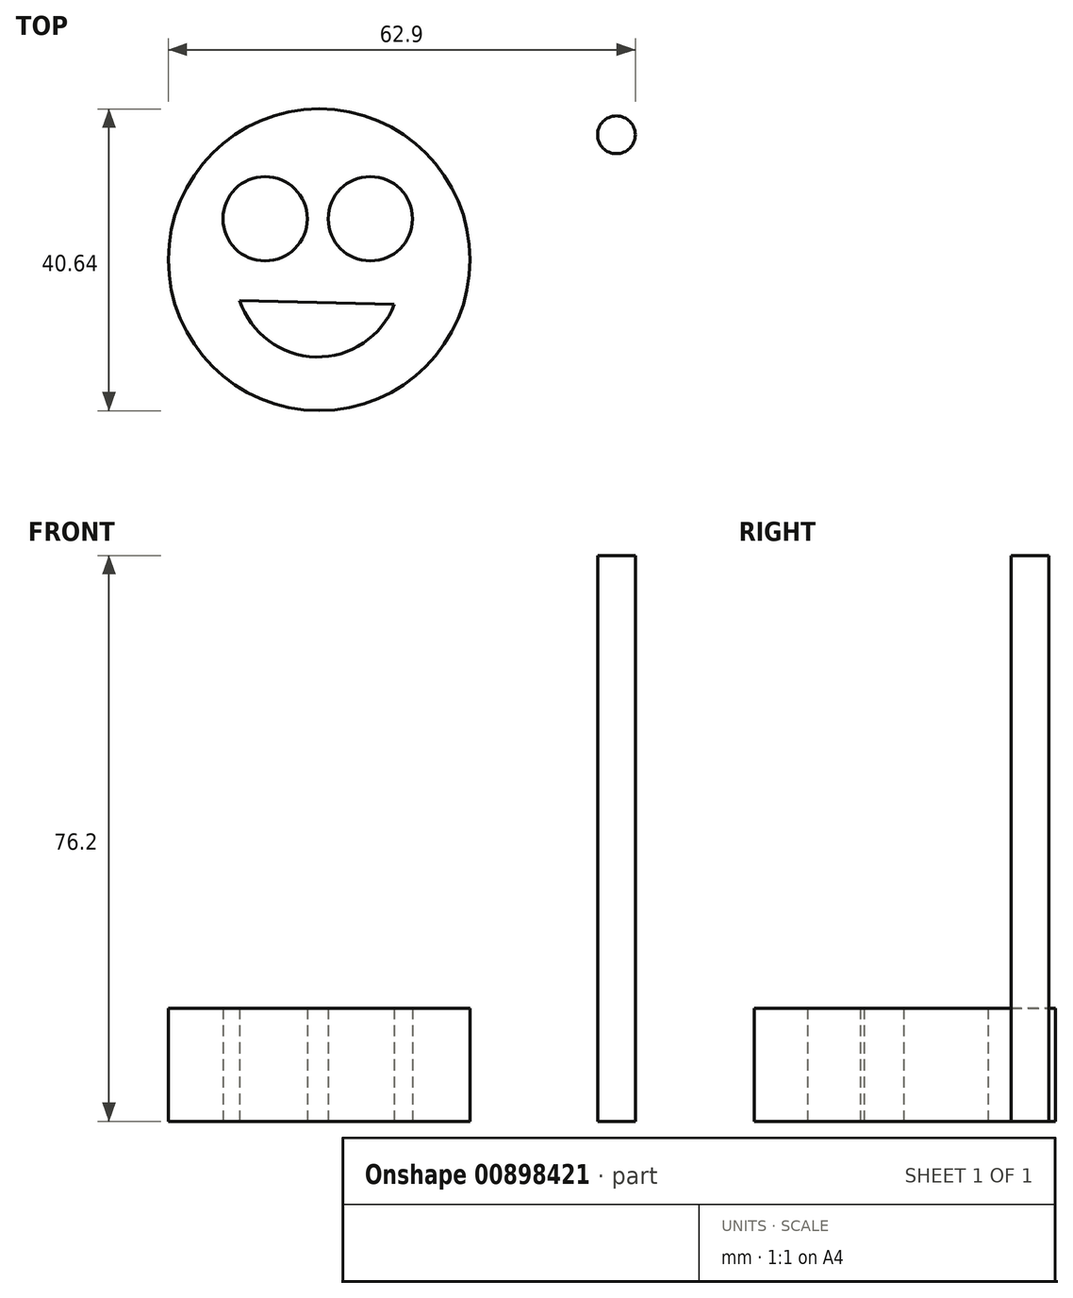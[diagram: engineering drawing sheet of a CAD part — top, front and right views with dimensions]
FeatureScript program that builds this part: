
annotation { "Feature Type Name" : "Feature", "Feature Type Description" : "" }
export const myFeature = defineFeature(function(context is Context, id is Id, definition is map)
    precondition{}
    {
        {
            var Q0;
            Q0=qCreatedBy(makeId("Top.planeOp"),FACE);
            var sketch = newSketch(context, id + "F0", { "sketchPlane" : qUnion([Q0])});
            skCircle(sketch, "E0", {"center": v(-17.17, 23.75) * mm, "radius": 20.32 * mm});
            skCircle(sketch, "E1", {"center": v(-10.28, 29.27) * mm, "radius": 5.68 * mm});
            skArc(sketch, "E2", {"start": v(-27.87, 18.26) * mm, "mid": v(-17.64, 10.67) * mm, "end": v(-7.05, 17.75) * mm});
            skLineSegment(sketch, "E3", {"start": v(-27.87, 18.26) * mm, "end": v(-7.05, 17.75) * mm});
            skLineSegment(sketch, "E4", {"start": v(-17.37, 21.73) * mm, "end": v(-17.37, 44.57) * mm});
            skCircle(sketch, "E5.MirrorC", {"center": v(-24.46, 29.27) * mm, "radius": 5.68 * mm});
            skCircle(sketch, "E6", {"center": v(-24.46, 29.27) * mm, "radius": 2.26 * mm});
            skCircle(sketch, "E7.MirrorC", {"center": v(-10.28, 29.27) * mm, "radius": 2.26 * mm});
            skSolve(sketch);
        }
        {
            var Q0;
            Q0=makeQuery(id+"F0.imprint","IMPRINT",FACE,{"disambiguationData":[TD([[makeQuery(id+"F0.imprint","IMPRINT",EDGE,{"derivedFrom":sQuery(id+"F0.wireOp",EDGE,"E0")}),1.0]])]});
            extrude(context, id + "F1", {"entities" : qUnion([Q0]), "depth" : 15.24 * mm, "offsetDistance" : 25.4 * mm});
        }
        {
            var Q0;
            Q0=qCreatedBy(makeId("Top.planeOp"),FACE);
            var sketch = newSketch(context, id + "F2", { "sketchPlane" : qUnion([Q0])});
            skCircle(sketch, "E8", {"center": v(22.87, 40.58) * mm, "radius": 2.54 * mm});
            skSolve(sketch);
        }
        {
            var Q0;
            Q0 = qSketchRegion(id + "F2", true);
            extrude(context, id + "F3", {"entities" : qUnion([Q0]), "depth" : 76.2 * mm, "offsetDistance" : 25.4 * mm});
        }
    });
